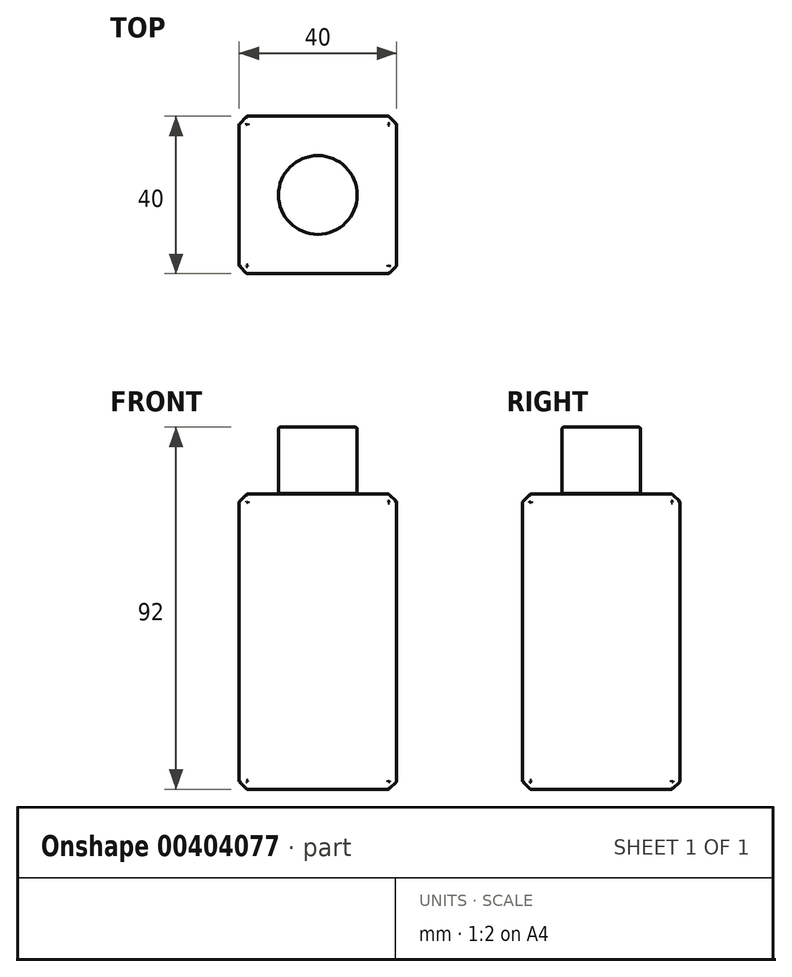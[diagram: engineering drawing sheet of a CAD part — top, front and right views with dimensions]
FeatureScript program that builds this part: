
annotation { "Feature Type Name" : "Feature", "Feature Type Description" : "" }
export const myFeature = defineFeature(function(context is Context, id is Id, definition is map)
    precondition{}
    {
        {
            var Q0;
            Q0=qCreatedBy(makeId("Top.planeOp"),FACE);
            var sketch = newSketch(context, id + "F0", { "sketchPlane" : qUnion([Q0])});
            skLineSegment(sketch, "E0.bottom", {"start": v(20, -20) * mm, "end": v(-20, -20) * mm});
            skLineSegment(sketch, "E0.top", {"start": v(20, 20) * mm, "end": v(-20, 20) * mm});
            skLineSegment(sketch, "E0.left", {"start": v(20, -20) * mm, "end": v(20, 20) * mm});
            skLineSegment(sketch, "E0.right", {"start": v(-20, -20) * mm, "end": v(-20, 20) * mm});
            skPoint(sketch, "E0.middle", {"position": v(0, 0) * mm});
            skCircle(sketch, "E1", {"center": v(0, 0) * mm, "radius": 10 * mm});
            skSolve(sketch);
        }
        {
            var Q0;
            Q0=makeQuery(id+"F0.imprint","IMPRINT",FACE,{"disambiguationData":[TD([[makeQuery(id+"F0.imprint","IMPRINT",EDGE,{"derivedFrom":sQuery(id+"F0.wireOp",EDGE,"E0.bottom")}),-1.0]])]});
            var Q1;
            Q1=makeQuery(id+"F0.imprint","IMPRINT",FACE,{"disambiguationData":[TD([[makeQuery(id+"F0.imprint","IMPRINT",EDGE,{"derivedFrom":sQuery(id+"F0.wireOp",EDGE,"E1")}),1.0]])]});
            extrude(context, id + "F1", {"entities" : qUnion([Q0, Q1]), "depth" : 75 * mm});
        }
        {
            var Q0;
            Q0=makeQuery(id+"F0.imprint","IMPRINT",FACE,{"disambiguationData":[TD([[makeQuery(id+"F0.imprint","IMPRINT",EDGE,{"derivedFrom":sQuery(id+"F0.wireOp",EDGE,"E1")}),1.0]])]});
            extrude(context, id + "F2", {"entities" : qUnion([Q0]), "depth" : 92 * mm, "hasSecondDirection" : true, "secondDirectionOppositeDirection" : false, "secondDirectionDepth" : 75.2 * mm});
        }
        {
            var Q0;
            Q0=makeQuery(id+"F1.opExtrude","SWEPT_FACE",FACE,{"disambiguationData":[OSD([sQuery(id+"F0.wireOp",EDGE,"E0.bottom")])]});
            var Q1;
            Q1=makeQuery(id+"F1.opExtrude","SWEPT_FACE",FACE,{"disambiguationData":[OSD([sQuery(id+"F0.wireOp",EDGE,"E0.right")])]});
            var Q2;
            Q2=makeQuery(id+"F1.opExtrude","SWEPT_FACE",FACE,{"disambiguationData":[OSD([sQuery(id+"F0.wireOp",EDGE,"E0.left")])]});
            var Q3;
            Q3=makeQuery(id+"F1.opExtrude","SWEPT_FACE",FACE,{"disambiguationData":[OSD([sQuery(id+"F0.wireOp",EDGE,"E0.top")])]});
            chamfer(context, id + "F3", {"entities" : qUnion([Q0, Q1, Q2, Q3]), "width" : 2 * mm, "tangentPropagation" : true});
        }
        {
            var Q0;
            Q0=makeQuery(id+"F2.opExtrude","CAP_FACE",FACE,{"disambiguationData":[OSD([sQuery(id+"F0.wireOp",EDGE,"E1")])],"isStart":false});
            fillet(context, id + "F4", {"entities" : qUnion([Q0]), "radius" : 0.5 * mm, "tangentPropagation" : true, "allowEdgeOverflow" : false});
        }
        {
            var Q0;
            {var subQ0=sQuery(id+"F0.wireOp",EDGE,"E0.right");Q0=makeQuery(id+"F3.opChamfer","BLEND_FACE",FACE,{"disambiguationData":[OSD([subQ0]),TDD([makeQuery(id+"F1.opExtrude","CAP_EDGE",EDGE,{"disambiguationData":[OSD([subQ0])],"isStart":false})])]});}
            var Q1;
            {var subQ0=sQuery(id+"F0.wireOp",EDGE,"E0.top");Q1=makeQuery(id+"F3.opChamfer","BLEND_FACE",FACE,{"disambiguationData":[OSD([subQ0]),TDD([makeQuery(id+"F1.opExtrude","CAP_EDGE",EDGE,{"disambiguationData":[OSD([subQ0])],"isStart":false})])]});}
            var Q2;
            {var subQ0=sQuery(id+"F0.wireOp",EDGE,"E0.right");var subQ1=sQuery(id+"F0.wireOp",EDGE,"E0.top");Q2=makeQuery(id+"F3.opChamfer","BLEND_FACE",FACE,{"disambiguationData":[OSD([subQ1,subQ0]),TDD([makeQuery(id+"F1.opExtrude","SWEPT_EDGE",EDGE,{"disambiguationData":[OSD([subQ1,subQ0])]})])]});}
            var Q3;
            {var subQ0=sQuery(id+"F0.wireOp",EDGE,"E0.bottom");Q3=makeQuery(id+"F3.opChamfer","BLEND_FACE",FACE,{"disambiguationData":[OSD([subQ0]),TDD([makeQuery(id+"F1.opExtrude","CAP_EDGE",EDGE,{"disambiguationData":[OSD([subQ0])],"isStart":false})])]});}
            var Q4;
            {var subQ0=sQuery(id+"F0.wireOp",EDGE,"E0.right");var subQ1=sQuery(id+"F0.wireOp",EDGE,"E0.bottom");Q4=makeQuery(id+"F3.opChamfer","BLEND_FACE",FACE,{"disambiguationData":[OSD([subQ1,subQ0]),TDD([makeQuery(id+"F1.opExtrude","SWEPT_EDGE",EDGE,{"disambiguationData":[OSD([subQ1,subQ0])]})])]});}
            var Q5;
            {var subQ0=sQuery(id+"F0.wireOp",EDGE,"E0.left");Q5=makeQuery(id+"F3.opChamfer","BLEND_FACE",FACE,{"disambiguationData":[OSD([subQ0]),TDD([makeQuery(id+"F1.opExtrude","CAP_EDGE",EDGE,{"disambiguationData":[OSD([subQ0])],"isStart":false})])]});}
            var Q6;
            {var subQ0=sQuery(id+"F0.wireOp",EDGE,"E0.left");var subQ1=sQuery(id+"F0.wireOp",EDGE,"E0.bottom");Q6=makeQuery(id+"F3.opChamfer","BLEND_FACE",FACE,{"disambiguationData":[OSD([subQ1,subQ0]),TDD([makeQuery(id+"F1.opExtrude","SWEPT_EDGE",EDGE,{"disambiguationData":[OSD([subQ1,subQ0])]})])]});}
            var Q7;
            {var subQ0=sQuery(id+"F0.wireOp",EDGE,"E0.left");Q7=makeQuery(id+"F3.opChamfer","BLEND_FACE",FACE,{"disambiguationData":[OSD([subQ0]),TDD([makeQuery(id+"F1.opExtrude","CAP_EDGE",EDGE,{"disambiguationData":[OSD([subQ0])],"isStart":true})])]});}
            var Q8;
            {var subQ0=sQuery(id+"F0.wireOp",EDGE,"E0.top");Q8=makeQuery(id+"F3.opChamfer","BLEND_FACE",FACE,{"disambiguationData":[OSD([subQ0]),TDD([makeQuery(id+"F1.opExtrude","CAP_EDGE",EDGE,{"disambiguationData":[OSD([subQ0])],"isStart":true})])]});}
            var Q9;
            {var subQ0=sQuery(id+"F0.wireOp",EDGE,"E0.left");var subQ1=sQuery(id+"F0.wireOp",EDGE,"E0.top");Q9=makeQuery(id+"F3.opChamfer","BLEND_FACE",FACE,{"disambiguationData":[OSD([subQ1,subQ0]),TDD([makeQuery(id+"F1.opExtrude","SWEPT_EDGE",EDGE,{"disambiguationData":[OSD([subQ1,subQ0])]})])]});}
            var Q10;
            {var subQ0=sQuery(id+"F0.wireOp",EDGE,"E0.bottom");Q10=makeQuery(id+"F3.opChamfer","BLEND_FACE",FACE,{"disambiguationData":[OSD([subQ0]),TDD([makeQuery(id+"F1.opExtrude","CAP_EDGE",EDGE,{"disambiguationData":[OSD([subQ0])],"isStart":true})])]});}
            var Q11;
            {var subQ0=sQuery(id+"F0.wireOp",EDGE,"E0.right");Q11=makeQuery(id+"F3.opChamfer","BLEND_FACE",FACE,{"disambiguationData":[OSD([subQ0]),TDD([makeQuery(id+"F1.opExtrude","CAP_EDGE",EDGE,{"disambiguationData":[OSD([subQ0])],"isStart":true})])]});}
            fillet(context, id + "F5", {"entities" : qUnion([Q0, Q1, Q2, Q3, Q4, Q5, Q6, Q7, Q8, Q9, Q10, Q11]), "radius" : 0.5 * mm, "allowEdgeOverflow" : false});
        }
    });
